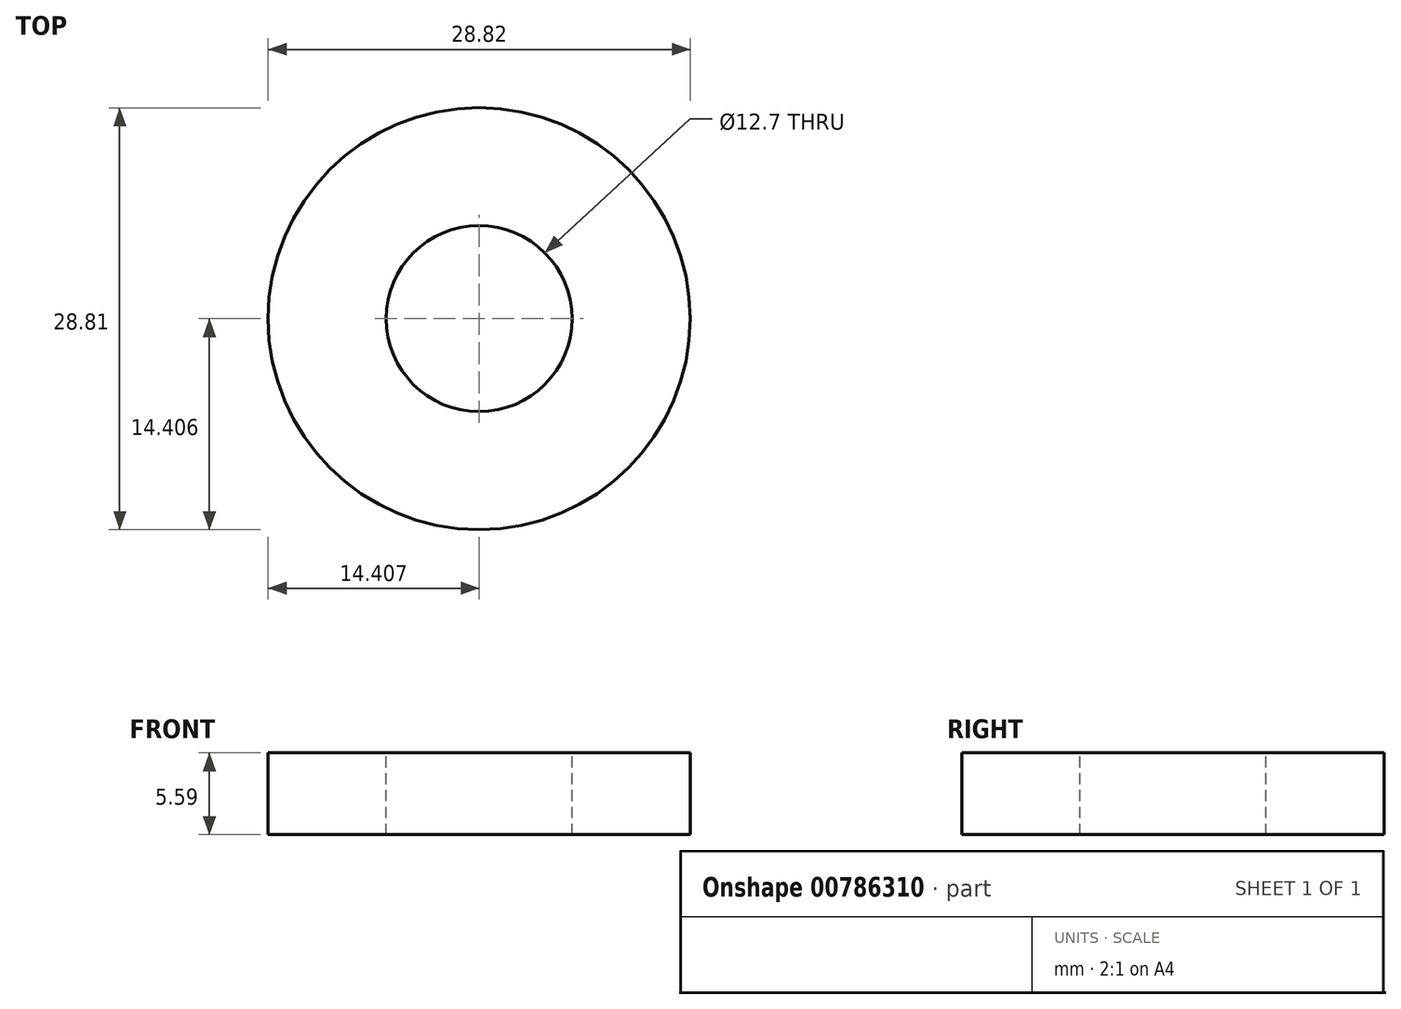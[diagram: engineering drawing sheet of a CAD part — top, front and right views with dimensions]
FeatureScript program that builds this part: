
annotation { "Feature Type Name" : "Feature", "Feature Type Description" : "" }
export const myFeature = defineFeature(function(context is Context, id is Id, definition is map)
    precondition{}
    {
        {
            var Q0;
            Q0=qCreatedBy(makeId("Top.planeOp"),FACE);
            var sketch = newSketch(context, id + "F0", { "sketchPlane" : qUnion([Q0])});
            skLineSegment(sketch, "E0.bottom", {"start": v(-73.92, -72.44) * mm, "end": v(75.28, -72.44) * mm});
            skLineSegment(sketch, "E0.top", {"start": v(-73.92, 67.32) * mm, "end": v(75.28, 67.32) * mm});
            skLineSegment(sketch, "E0.left", {"start": v(-73.92, -72.44) * mm, "end": v(-73.92, 67.32) * mm});
            skLineSegment(sketch, "E0.right", {"start": v(75.28, -72.44) * mm, "end": v(75.28, 67.32) * mm});
            skLineSegment(sketch, "E1", {"start": v(0, 0) * mm, "end": v(0, -72.44) * mm});
            skLineSegment(sketch, "E2", {"start": v(-50.47, -72.44) * mm, "end": v(-50.47, -64.83) * mm});
            skLineSegment(sketch, "E3", {"start": v(-50.47, -64.83) * mm, "end": v(-24.4, -64.83) * mm});
            skLineSegment(sketch, "E4", {"start": v(-24.4, -64.83) * mm, "end": v(-24.4, -72.44) * mm});
            skCircle(sketch, "E5", {"center": v(-41.53, -27.05) * mm, "radius": 14.4 * mm});
            skSolve(sketch);
        }
        {
            var Q0;
            Q0=makeQuery(id+"F0.imprint","IMPRINT",FACE,{"disambiguationData":[TD([[makeQuery(id+"F0.imprint","IMPRINT",EDGE,{"derivedFrom":sQuery(id+"F0.wireOp",EDGE,"E5")}),1.0]])]});
            extrude(context, id + "F1", {"entities" : qUnion([Q0]), "depth" : 5.6 * mm, "offsetDistance" : 25.4 * mm});
        }
        {
            var Q0;
            Q0=makeQuery(id+"F1.opExtrude","CAP_FACE",FACE,{"disambiguationData":[OSD([sQuery(id+"F0.wireOp",EDGE,"E5")])],"isStart":false});
            var sketch = newSketch(context, id + "F2", { "sketchPlane" : qUnion([Q0])});
            skPoint(sketch, "E6", {"position": v(-41.53, -27.05) * mm});
            skSolve(sketch);
        }
        {
            var Q0;
            Q0=sQuery(id+"F2.wireOp",VERTEX,"E6");
            var Q1;
            Q1=makeQuery(id+"F1.opExtrude","SWEPT_BODY",BODY,{"disambiguationData":[OSD([sQuery(id+"F0.wireOp",EDGE,"E5")])]});
            hole(context, id + "F3", {"style" : HoleStyle.C_BORE, "endStyle" : HoleEndStyle.THROUGH, "holeDiameter" : 11.43 * mm, "cBoreDiameter" : 12.7 * mm, "cBoreDepth" : 6.35 * mm, "majorDiameter" : 6.35 * mm, "isTappedThrough" : true, "tappedDepth" : 12.7 * mm, "tapClearance" : 3, "locations" : qUnion([Q0]), "scope" : qUnion([Q1])});
        }
    });
